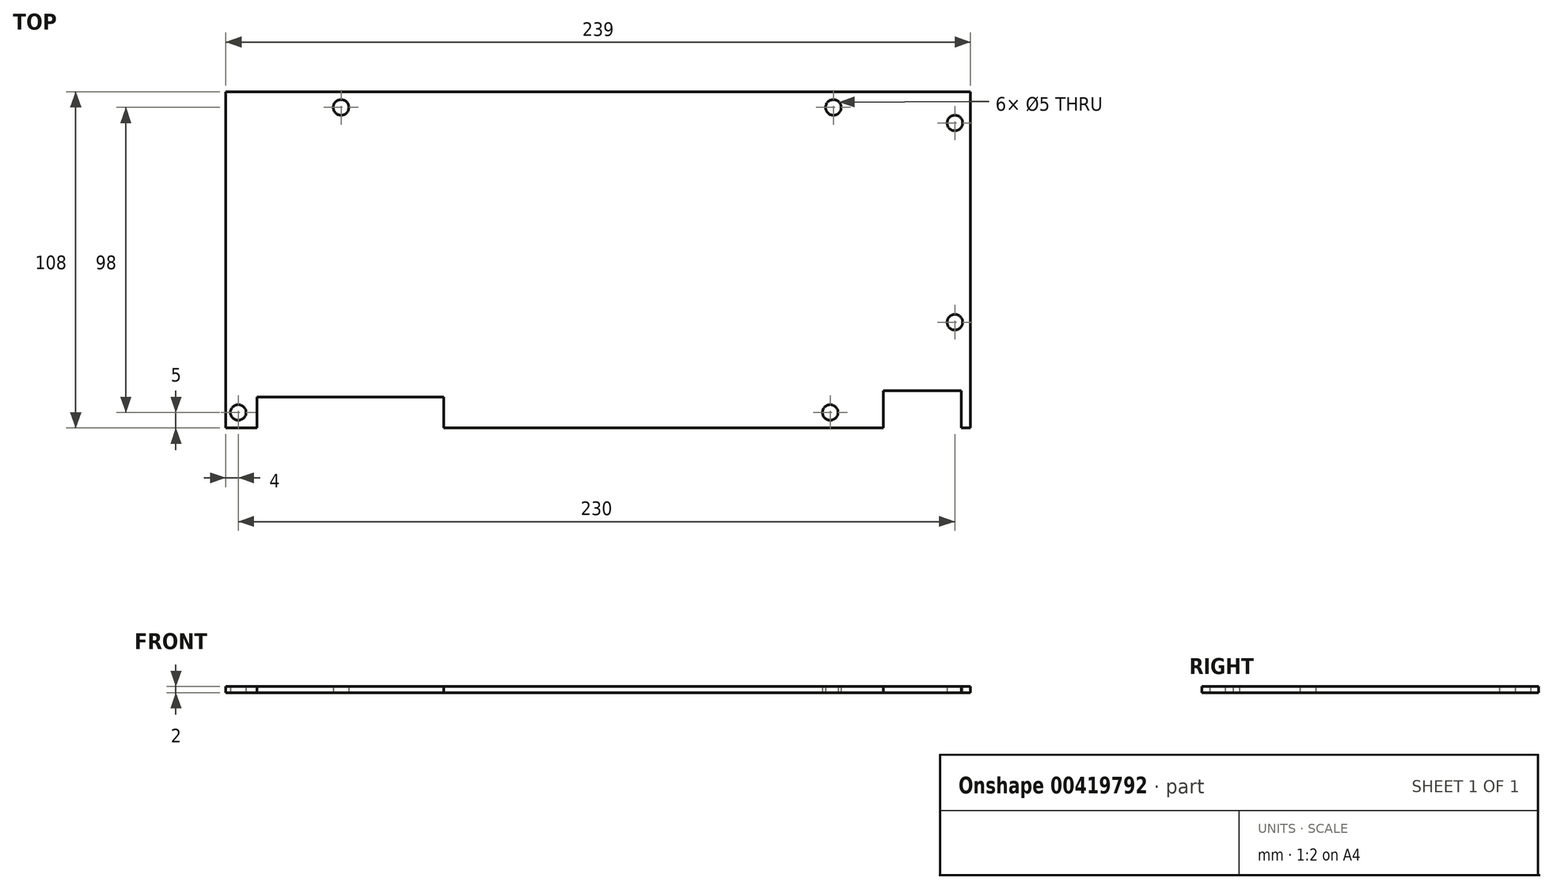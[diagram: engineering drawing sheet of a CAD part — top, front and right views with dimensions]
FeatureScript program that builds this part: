
annotation { "Feature Type Name" : "Feature", "Feature Type Description" : "" }
export const myFeature = defineFeature(function(context is Context, id is Id, definition is map)
    precondition{}
    {
        {
            var Q0;
            Q0=qCreatedBy(makeId("Top.planeOp"),FACE);
            var sketch = newSketch(context, id + "F0", { "sketchPlane" : qUnion([Q0])});
            skLineSegment(sketch, "E0.bottom", {"start": v(0, 0) * mm, "end": v(239, 0) * mm});
            skLineSegment(sketch, "E0.top", {"start": v(0, -108) * mm, "end": v(10, -108) * mm});
            skLineSegment(sketch, "E0.left", {"start": v(0, 0) * mm, "end": v(0, -108) * mm});
            skLineSegment(sketch, "E0.right", {"start": v(239, 0) * mm, "end": v(239, -108) * mm});
            skCircle(sketch, "E1", {"center": v(4, -103) * mm, "radius": 2.5 * mm});
            skCircle(sketch, "E2", {"center": v(194, -103) * mm, "radius": 2.5 * mm});
            skCircle(sketch, "E3", {"center": v(234, -74) * mm, "radius": 2.5 * mm});
            skCircle(sketch, "E4", {"center": v(234, -10) * mm, "radius": 2.5 * mm});
            skCircle(sketch, "E5", {"center": v(195, -5) * mm, "radius": 2.5 * mm});
            skCircle(sketch, "E6", {"center": v(37, -5) * mm, "radius": 2.5 * mm});
            skLineSegment(sketch, "E7", {"start": v(10, -108) * mm, "end": v(10, -98) * mm});
            skLineSegment(sketch, "E8", {"start": v(10, -98) * mm, "end": v(70, -98) * mm});
            skLineSegment(sketch, "E9", {"start": v(70, -98) * mm, "end": v(70, -108) * mm});
            skLineSegment(sketch, "E10.trimOffspring", {"start": v(70, -108) * mm, "end": v(211, -108) * mm});
            skLineSegment(sketch, "E11", {"start": v(236, -108) * mm, "end": v(236, -96) * mm});
            skLineSegment(sketch, "E12", {"start": v(236, -96) * mm, "end": v(211, -96) * mm});
            skLineSegment(sketch, "E13", {"start": v(211, -96) * mm, "end": v(211, -108) * mm});
            skLineSegment(sketch, "E14.trimOffspring", {"start": v(236, -108) * mm, "end": v(239, -108) * mm});
            skSolve(sketch);
        }
        {
            var Q0;
            Q0=makeQuery(id+"F0.imprint","IMPRINT",FACE,{"disambiguationData":[TD([[makeQuery(id+"F0.imprint","IMPRINT",EDGE,{"derivedFrom":sQuery(id+"F0.wireOp",EDGE,"E0.bottom")}),-1.0]])]});
            extrude(context, id + "F1", {"entities" : qUnion([Q0]), "depth" : 2 * mm});
        }
    });
